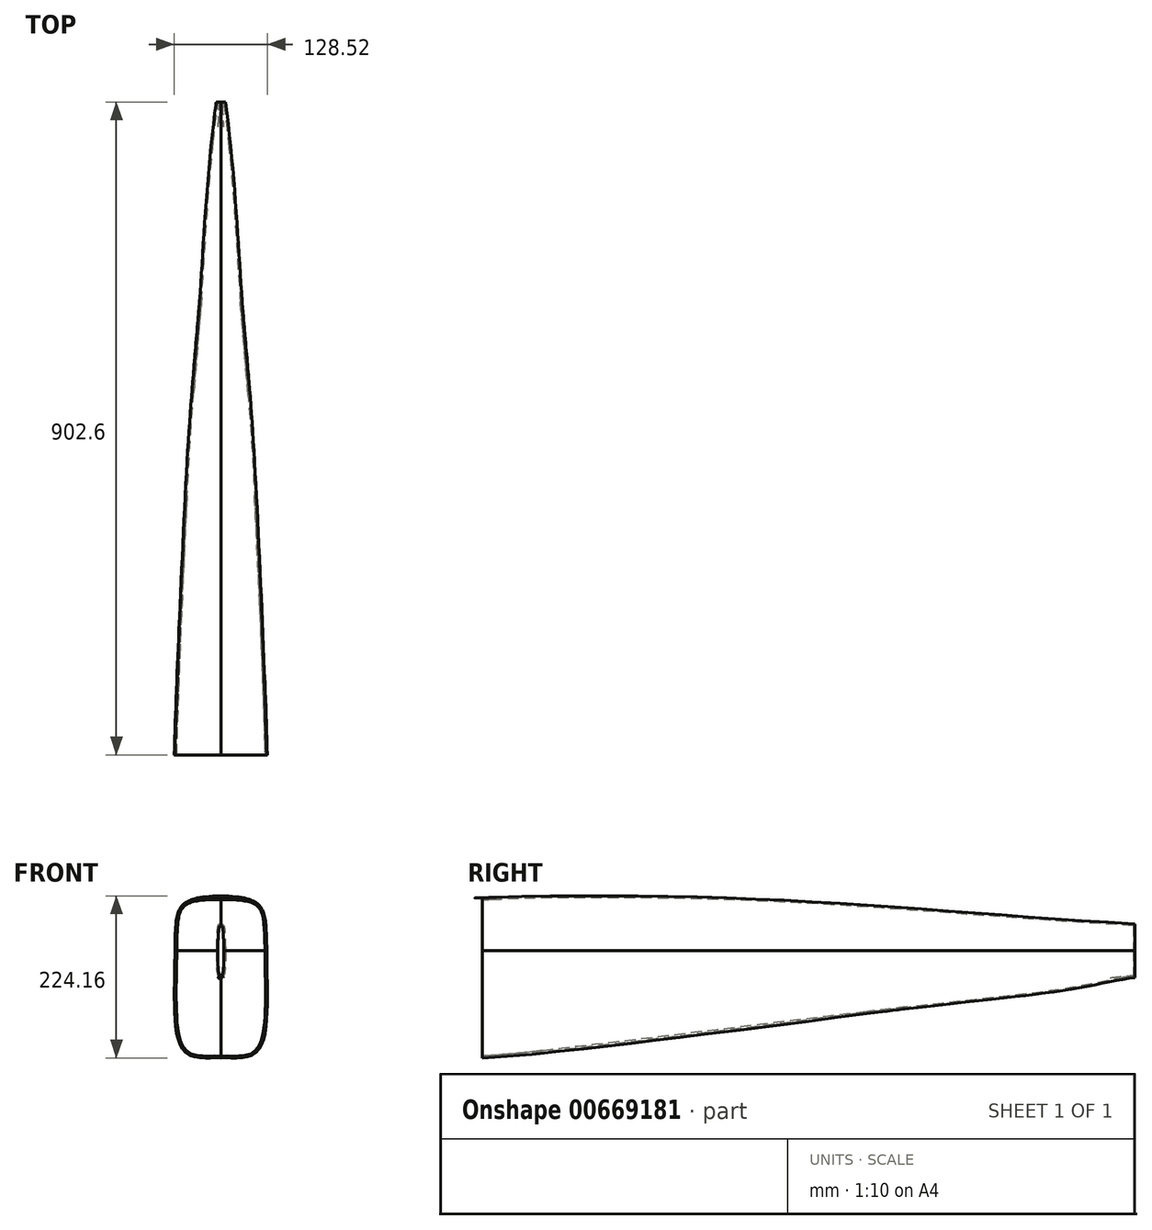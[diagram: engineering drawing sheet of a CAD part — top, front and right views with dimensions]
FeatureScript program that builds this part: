
annotation { "Feature Type Name" : "Feature", "Feature Type Description" : "" }
export const myFeature = defineFeature(function(context is Context, id is Id, definition is map)
    precondition{}
    {
        {
            var Q0;
            Q0=qCreatedBy(makeId("Right.planeOp"),FACE);
            var sketch = newSketch(context, id + "F0", { "sketchPlane" : qUnion([Q0])});
            skFitSpline(sketch, "E0", {"points": [v(-291.2, 32.25) * mm, v(-182.77, 59.08) * mm, v(335.99, 72.73) * mm, v(902.6, 36.73) * mm], "startDerivative": vector(465.19, 162.33) * mm, "endDerivative": vector(1346.22, -73.92) * mm});
            skLineSegment(sketch, "E1", {"start": v(0, 0) * mm, "end": v(-291.2, 0) * mm});
            skLineSegment(sketch, "E2", {"start": v(0, 0) * mm, "end": v(902.6, 0) * mm});
            skLineSegment(sketch, "E3", {"start": v(902.6, 36.73) * mm, "end": v(902.6, 0) * mm});
            skFitSpline(sketch, "E4", {"points": [v(-348.35, 0) * mm, v(-316.7, -80.48) * mm, v(-278.42, -111.32) * mm, v(-235.85, -128.25) * mm, v(-183.22, -140.6) * mm, v(-109.55, -149.3) * mm, v(-23.65, -149.47) * mm, v(64.6, -143) * mm, v(620.02, -76.78) * mm, v(822.7, -52.15) * mm, v(902.6, -37.5) * mm], "startDerivative": vector(0, -1542.5) * mm, "endDerivative": vector(796.58, 90.74) * mm});
            skLineSegment(sketch, "E5", {"start": v(902.6, 0) * mm, "end": v(902.6, -37.5) * mm});
            skLineSegment(sketch, "E6", {"start": v(0, 0) * mm, "end": v(0, 72.8) * mm});
            skLineSegment(sketch, "E7", {"start": v(0, 0) * mm, "end": v(0, -148.54) * mm});
            skLineSegment(sketch, "E8", {"start": v(-291.2, 0) * mm, "end": v(-348.35, 0) * mm});
            skLineSegment(sketch, "E9", {"start": v(-291.2, 32.25) * mm, "end": v(-291.2, 0) * mm});
            skLineSegment(sketch, "E10", {"start": v(0, 72.8) * mm, "end": v(0, 72.8) * mm});
            skLineSegment(sketch, "E11", {"start": v(0, -148.54) * mm, "end": v(0, -148.54) * mm});
            skSolve(sketch);
        }
        {
            var Q0;
            Q0=qCreatedBy(makeId("Top.planeOp"),FACE);
            var sketch = newSketch(context, id + "F1", { "sketchPlane" : qUnion([Q0])});
            skLineSegment(sketch, "E12.0", {"start": v(0, 0) * mm, "end": v(0, 902.6) * mm});
            skLineSegment(sketch, "E12.1", {"start": v(0, 0) * mm, "end": v(0, -348.35) * mm});
            skFitSpline(sketch, "E13", {"points": [v(0, -348.35) * mm, v(59.54, -145.17) * mm, v(63.5, 0) * mm, v(44.62, 439.02) * mm, v(29.68, 624.33) * mm, v(6.35, 902.6) * mm], "startDerivative": vector(598.07, 0) * mm, "endDerivative": vector(-185.5, 1334.66) * mm});
            skLineSegment(sketch, "E14", {"start": v(6.35, 902.6) * mm, "end": v(0, 902.6) * mm});
            skFitSpline(sketch, "E15.MirrorCS", {"points": [v(0, -348.35) * mm, v(-59.54, -145.17) * mm, v(-63.5, 0) * mm, v(-44.62, 439.02) * mm, v(-29.68, 624.33) * mm, v(-6.35, 902.6) * mm], "startDerivative": vector(-598.07, 0) * mm, "endDerivative": vector(185.5, 1334.66) * mm});
            skLineSegment(sketch, "E16.MirrorCS", {"start": v(-6.35, 902.6) * mm, "end": v(0, 902.6) * mm});
            skLineSegment(sketch, "E17", {"start": v(63.5, 0) * mm, "end": v(-63.5, 0) * mm});
            skFitSpline(sketch, "E18", {"points": [v(0, -348.35) * mm, v(59.54, -145.17) * mm, v(63.5, 0) * mm, v(44.62, 439.02) * mm, v(29.68, 624.33) * mm, v(6.35, 902.6) * mm], "startDerivative": vector(598.07, 0) * mm, "endDerivative": vector(-185.5, 1334.66) * mm});
            skPoint(sketch, "E19.orphan", {"position": v(0, -291.2) * mm});
            skSolve(sketch);
        }
        {
            var Q0;
            Q0=qCreatedBy(makeId("Front.planeOp"),FACE);
            var sketch = newSketch(context, id + "F2", { "sketchPlane" : qUnion([Q0])});
            skLineSegment(sketch, "E20.0", {"start": v(0, 0) * mm, "end": v(0, 72.8) * mm});
            skLineSegment(sketch, "E20.1", {"start": v(0, 0) * mm, "end": v(0, -148.54) * mm});
            skLineSegment(sketch, "E21.0", {"start": v(63.5, 0) * mm, "end": v(-63.5, 0) * mm});
            skFitSpline(sketch, "E22", {"points": [v(0, 72.8) * mm, v(49.79, 65.25) * mm, v(62.4, 32.72) * mm, v(63.5, 0) * mm], "startDerivative": vector(108.53, 0.33) * mm, "endDerivative": vector(0, -85.93) * mm});
            skFitSpline(sketch, "E23", {"points": [v(63.5, 0) * mm, v(63.85, -84) * mm, v(46.29, -143.06) * mm, v(0, -148.54) * mm], "startDerivative": vector(0, -170.4) * mm, "endDerivative": vector(-145.42, -8.24) * mm});
            skFitSpline(sketch, "E24.MirrorCS", {"points": [v(0, 72.8) * mm, v(-49.79, 65.25) * mm, v(-62.4, 32.72) * mm, v(-63.5, 0) * mm], "startDerivative": vector(-108.53, 0.33) * mm, "endDerivative": vector(0, -85.93) * mm});
            skFitSpline(sketch, "E25.MirrorCS", {"points": [v(-63.5, 0) * mm, v(-63.85, -84) * mm, v(-46.29, -143.06) * mm, v(0, -148.54) * mm], "startDerivative": vector(0, -170.4) * mm, "endDerivative": vector(145.42, -8.24) * mm});
            skSolve(sketch);
        }
        {
            var Q0;
            Q0=qCreatedBy(makeId("Front.planeOp"),FACE);
            var Q1;
            Q1=sQuery(id+"F0.wireOp",VERTEX,"E2.end");
            cPlane(context, id + "F3", {"entities" : qUnion([Q0, Q1]), "cplaneType" : CPlaneType.PLANE_POINT, "offset" : 25.4 * mm, "width" : 152.4 * mm, "height" : 152.4 * mm});
        }
        {
            var Q0;
            Q0=qCreatedBy(id+"F3.planeOp",FACE);
            var sketch = newSketch(context, id + "F4", { "sketchPlane" : qUnion([Q0])});
            skLineSegment(sketch, "E26.0", {"start": v(0, 36.73) * mm, "end": v(0, 0) * mm});
            skLineSegment(sketch, "E26.1", {"start": v(6.35, 0) * mm, "end": v(0, 0) * mm});
            skLineSegment(sketch, "E26.2", {"start": v(0, 0) * mm, "end": v(0, -37.5) * mm});
            skLineSegment(sketch, "E26.3", {"start": v(-6.35, 0) * mm, "end": v(0, 0) * mm});
            skFitSpline(sketch, "E27", {"points": [v(0, 36.73) * mm, v(3.5, 35.28) * mm, v(6.07, 16.88) * mm, v(6.35, 0) * mm], "startDerivative": vector(22.86, 0) * mm, "endDerivative": vector(0, -34.83) * mm});
            skFitSpline(sketch, "E28", {"points": [v(6.35, 0) * mm, v(5.57, -28.45) * mm, v(2.92, -36.74) * mm, v(0, -37.5) * mm], "startDerivative": vector(0, -47.63) * mm, "endDerivative": vector(-23.06, 0) * mm});
            skFitSpline(sketch, "E29.MirrorCS", {"points": [v(-6.35, 0) * mm, v(-5.57, -28.45) * mm, v(-2.92, -36.74) * mm, v(0, -37.5) * mm], "startDerivative": vector(0, -47.63) * mm, "endDerivative": vector(23.06, 0) * mm});
            skFitSpline(sketch, "E30.MirrorCS", {"points": [v(0, 36.73) * mm, v(-3.5, 35.28) * mm, v(-6.07, 16.88) * mm, v(-6.35, 0) * mm], "startDerivative": vector(-22.86, 0) * mm, "endDerivative": vector(0, -34.83) * mm});
            skSolve(sketch);
        }
        {
            var Q0;
            {var subQ0=sQuery(id+"F1.wireOp",EDGE,"E12.0");Q0=makeQuery(id+"F1.imprint","IMPRINT",FACE,{"disambiguationData":[TD([[makeQuery(id+"F1.imprint","IMPRINT",EDGE,{"derivedFrom":subQ0}),-1.0]])]});}
            var Q1;
            Q1=makeQuery(id+"F0.imprint","IMPRINT",FACE,{"disambiguationData":[TD([[makeQuery(id+"F0.imprint","IMPRINT",EDGE,{"derivedFrom":sQuery(id+"F0.wireOp",EDGE,"E2")}),-1.0]])]});
            var Q2;
            Q2=sQuery(id+"F2.wireOp",EDGE,"E23");
            var Q3;
            Q3=sQuery(id+"F4.wireOp",EDGE,"E28");
            loft(context, id + "F5", {"addGuides" : true, "sheetProfilesArray" : [{ "sheetProfileEntities" : qUnion([Q0]) }, { "sheetProfileEntities" : qUnion([Q1]) }], "guidesArray" : [{ "guideEntities" : qUnion([Q2]), "guideDerivativeType" : LoftGuideDerivativeType.DEFAULT, "guideDerivativeMagnitude" : 1 }, { "guideEntities" : qUnion([Q3]), "guideDerivativeType" : LoftGuideDerivativeType.DEFAULT, "guideDerivativeMagnitude" : 1 }]});
        }
        {
            var Q1;
            {var subQ0=sQuery(id+"F1.wireOp",EDGE,"E12.0");Q1=makeQuery(id+"F1.imprint","IMPRINT",FACE,{"disambiguationData":[TD([[makeQuery(id+"F1.imprint","IMPRINT",EDGE,{"derivedFrom":subQ0}),1.0]])]});}
            var Q2;
            Q2=makeQuery(id+"F0.imprint","IMPRINT",FACE,{"disambiguationData":[TD([[makeQuery(id+"F0.imprint","IMPRINT",EDGE,{"derivedFrom":sQuery(id+"F0.wireOp",EDGE,"E2")}),-1.0]])]});
            var Q3;
            Q3=sQuery(id+"F2.wireOp",EDGE,"E25.MirrorCS");
            var Q4;
            Q4=sQuery(id+"F4.wireOp",EDGE,"E29.MirrorCS");
            loft(context, id + "F6", {"operationType" : NewBodyOperationType.ADD, "addGuides" : true, "sheetProfilesArray" : [{ "sheetProfileEntities" : qUnion([Q1]) }, { "sheetProfileEntities" : qUnion([Q2]) }], "guidesArray" : [{ "guideEntities" : qUnion([Q3]), "guideDerivativeType" : LoftGuideDerivativeType.DEFAULT, "guideDerivativeMagnitude" : 1 }, { "guideEntities" : qUnion([Q4]), "guideDerivativeType" : LoftGuideDerivativeType.DEFAULT, "guideDerivativeMagnitude" : 1 }]});
        }
        {
            var Q1;
            Q1=makeQuery(id+"F0.imprint","IMPRINT",FACE,{"disambiguationData":[TD([[makeQuery(id+"F0.imprint","IMPRINT",EDGE,{"derivedFrom":sQuery(id+"F0.wireOp",EDGE,"E2")}),1.0]])]});
            var Q2;
            {var subQ0=sQuery(id+"F1.wireOp",EDGE,"E12.0");Q2=makeQuery(id+"F1.imprint","IMPRINT",FACE,{"disambiguationData":[TD([[makeQuery(id+"F1.imprint","IMPRINT",EDGE,{"derivedFrom":subQ0}),1.0]])]});}
            var Q3;
            Q3=sQuery(id+"F2.wireOp",EDGE,"E24.MirrorCS");
            var Q4;
            Q4=sQuery(id+"F4.wireOp",EDGE,"E30.MirrorCS");
            loft(context, id + "F7", {"operationType" : NewBodyOperationType.ADD, "addGuides" : true, "sheetProfilesArray" : [{ "sheetProfileEntities" : qUnion([Q1]) }, { "sheetProfileEntities" : qUnion([Q2]) }], "guidesArray" : [{ "guideEntities" : qUnion([Q3]), "guideDerivativeType" : LoftGuideDerivativeType.DEFAULT, "guideDerivativeMagnitude" : 1 }, { "guideEntities" : qUnion([Q4]), "guideDerivativeType" : LoftGuideDerivativeType.DEFAULT, "guideDerivativeMagnitude" : 1 }]});
        }
        {
            var Q1;
            Q1=makeQuery(id+"F0.imprint","IMPRINT",FACE,{"disambiguationData":[TD([[makeQuery(id+"F0.imprint","IMPRINT",EDGE,{"derivedFrom":sQuery(id+"F0.wireOp",EDGE,"E2")}),1.0]])]});
            var Q2;
            {var subQ0=sQuery(id+"F1.wireOp",EDGE,"E12.0");Q2=makeQuery(id+"F1.imprint","IMPRINT",FACE,{"disambiguationData":[TD([[makeQuery(id+"F1.imprint","IMPRINT",EDGE,{"derivedFrom":subQ0}),-1.0]])]});}
            var Q3;
            Q3=sQuery(id+"F2.wireOp",EDGE,"E22");
            var Q4;
            Q4=sQuery(id+"F4.wireOp",EDGE,"E27");
            loft(context, id + "F8", {"operationType" : NewBodyOperationType.ADD, "addGuides" : true, "sheetProfilesArray" : [{ "sheetProfileEntities" : qUnion([Q1]) }, { "sheetProfileEntities" : qUnion([Q2]) }], "guidesArray" : [{ "guideEntities" : qUnion([Q3]), "guideDerivativeType" : LoftGuideDerivativeType.DEFAULT, "guideDerivativeMagnitude" : 1 }, { "guideEntities" : qUnion([Q4]), "guideDerivativeType" : LoftGuideDerivativeType.DEFAULT, "guideDerivativeMagnitude" : 1 }]});
        }
        {
            var Q0;
            {var subQ0=sQuery(id+"F1.wireOp",EDGE,"E18");var subQ1=sQuery(id+"F1.wireOp",EDGE,"E17");var subQ2=sQuery(id+"F1.wireOp",EDGE,"E12.1");var subQ3=sQuery(id+"F1.wireOp",EDGE,"E12.0");var subQ4=sQuery(id+"F0.wireOp",EDGE,"E7");var subQ5=sQuery(id+"F0.wireOp",EDGE,"E6");var subQ6=sQuery(id+"F0.wireOp",EDGE,"E2");var subQ7=sQuery(id+"F0.wireOp",EDGE,"E1");var subQ8=sQuery(id+"F0.wireOp",EDGE,"E4");Q0=makeQuery(id+"F8.boolean.opBoolean","MERGE",FACE,{"derivedFrom":[makeQuery(id+"F7.boolean.opBoolean","MERGE",FACE,{"derivedFrom":[makeQuery(id+"F6.boolean.opBoolean","MERGE",FACE,{"derivedFrom":[makeQuery(id+"F5.opLoft","SWEPT_FACE",FACE,{"disambiguationData":[OSD([subQ7,subQ6,subQ5,subQ4,subQ8,subQ3,subQ2,subQ1,subQ0,sQuery(id+"F2.wireOp",EDGE,"E23")])]}),makeQuery(id+"F6.opLoft","SWEPT_FACE",FACE,{"disambiguationData":[OSD([subQ7,subQ6,subQ5,subQ4,subQ8,subQ3,subQ2,subQ1,sQuery(id+"F2.wireOp",EDGE,"E25.MirrorCS")])]})]}),makeQuery(id+"F7.opLoft","SWEPT_FACE",FACE,{"disambiguationData":[OSD([subQ7,subQ6,subQ5,subQ4,subQ3,subQ2,subQ1,sQuery(id+"F2.wireOp",EDGE,"E24.MirrorCS")])]})]}),makeQuery(id+"F8.opLoft","SWEPT_FACE",FACE,{"disambiguationData":[OSD([subQ7,subQ6,subQ5,subQ4,subQ3,subQ2,subQ1,subQ0,sQuery(id+"F2.wireOp",EDGE,"E22")])]})]});}
            shell(context, id + "F9", {"entities" : qUnion([Q0]), "thickness" : 2.54 * mm});
        }
    });
